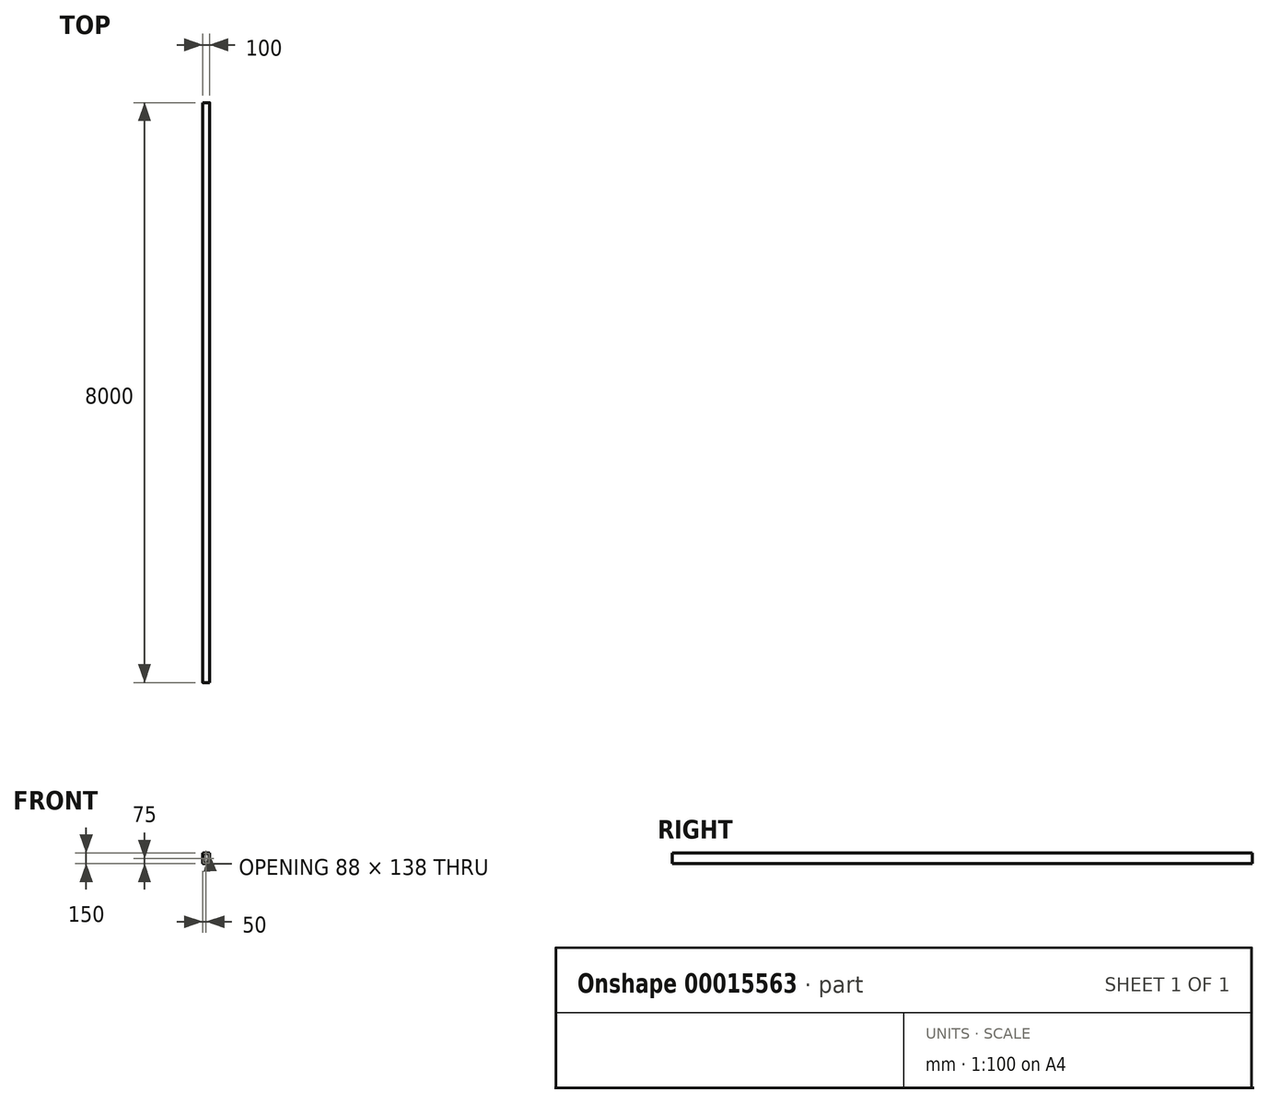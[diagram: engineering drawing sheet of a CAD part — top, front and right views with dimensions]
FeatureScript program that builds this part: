
annotation { "Feature Type Name" : "Feature", "Feature Type Description" : "" }
export const myFeature = defineFeature(function(context is Context, id is Id, definition is map)
    precondition{}
    {
        {
            var Q0;
            Q0=qCreatedBy(makeId("Front.planeOp"),FACE);
            var sketch = newSketch(context, id + "F0", { "sketchPlane" : qUnion([Q0])});
            skLineSegment(sketch, "E0.bottom", {"start": v(-35, 75) * mm, "end": v(35, 75) * mm});
            skLineSegment(sketch, "E0.top", {"start": v(-35, -75) * mm, "end": v(35, -75) * mm});
            skLineSegment(sketch, "E0.left", {"start": v(-50, 60) * mm, "end": v(-50, -60) * mm});
            skLineSegment(sketch, "E0.right", {"start": v(50, 60) * mm, "end": v(50, -60) * mm});
            skPoint(sketch, "E0.middle", {"position": v(0, 0) * mm});
            skPoint(sketch, "E1.visualSharp", {"position": v(-50, 75) * mm});
            skArc(sketch, "E1.filletArc", {"start": v(-35, 75) * mm, "mid": v(-45.6, 70.6) * mm, "end": v(-50, 60) * mm});
            skPoint(sketch, "E2.visualSharp", {"position": v(50, 75) * mm});
            skArc(sketch, "E2.filletArc", {"start": v(50, 60) * mm, "mid": v(45.6, 70.6) * mm, "end": v(35, 75) * mm});
            skPoint(sketch, "E3.visualSharp", {"position": v(50, -75) * mm});
            skArc(sketch, "E3.filletArc", {"start": v(35, -75) * mm, "mid": v(45.6, -70.6) * mm, "end": v(50, -60) * mm});
            skPoint(sketch, "E4.visualSharp", {"position": v(-50, -75) * mm});
            skArc(sketch, "E4.filletArc", {"start": v(-50, -60) * mm, "mid": v(-45.6, -70.6) * mm, "end": v(-35, -75) * mm});
            skArc(sketch, "E5.0", {"start": v(-44, -60) * mm, "mid": v(-41.36, -66.36) * mm, "end": v(-35, -69) * mm});
            skLineSegment(sketch, "E5.1", {"start": v(-44, 60) * mm, "end": v(-44, -60) * mm});
            skLineSegment(sketch, "E5.2", {"start": v(-35, -69) * mm, "end": v(35, -69) * mm});
            skArc(sketch, "E5.3", {"start": v(-35, 69) * mm, "mid": v(-41.36, 66.36) * mm, "end": v(-44, 60) * mm});
            skArc(sketch, "E5.4", {"start": v(35, -69) * mm, "mid": v(41.36, -66.36) * mm, "end": v(44, -60) * mm});
            skLineSegment(sketch, "E5.5", {"start": v(44, 60) * mm, "end": v(44, -60) * mm});
            skArc(sketch, "E5.6", {"start": v(44, 60) * mm, "mid": v(41.36, 66.36) * mm, "end": v(35, 69) * mm});
            skLineSegment(sketch, "E5.7", {"start": v(-35, 69) * mm, "end": v(35, 69) * mm});
            skSolve(sketch);
        }
        {
            var Q0;
            Q0=makeQuery(id+"F0.imprint","IMPRINT",FACE,{"disambiguationData":[TD([[makeQuery(id+"F0.imprint","IMPRINT",EDGE,{"derivedFrom":sQuery(id+"F0.wireOp",EDGE,"E0.bottom")}),-1.0]])]});
            extrude(context, id + "F1", {"entities" : qUnion([Q0]), "depth" : 8000 * mm});
        }
    });
